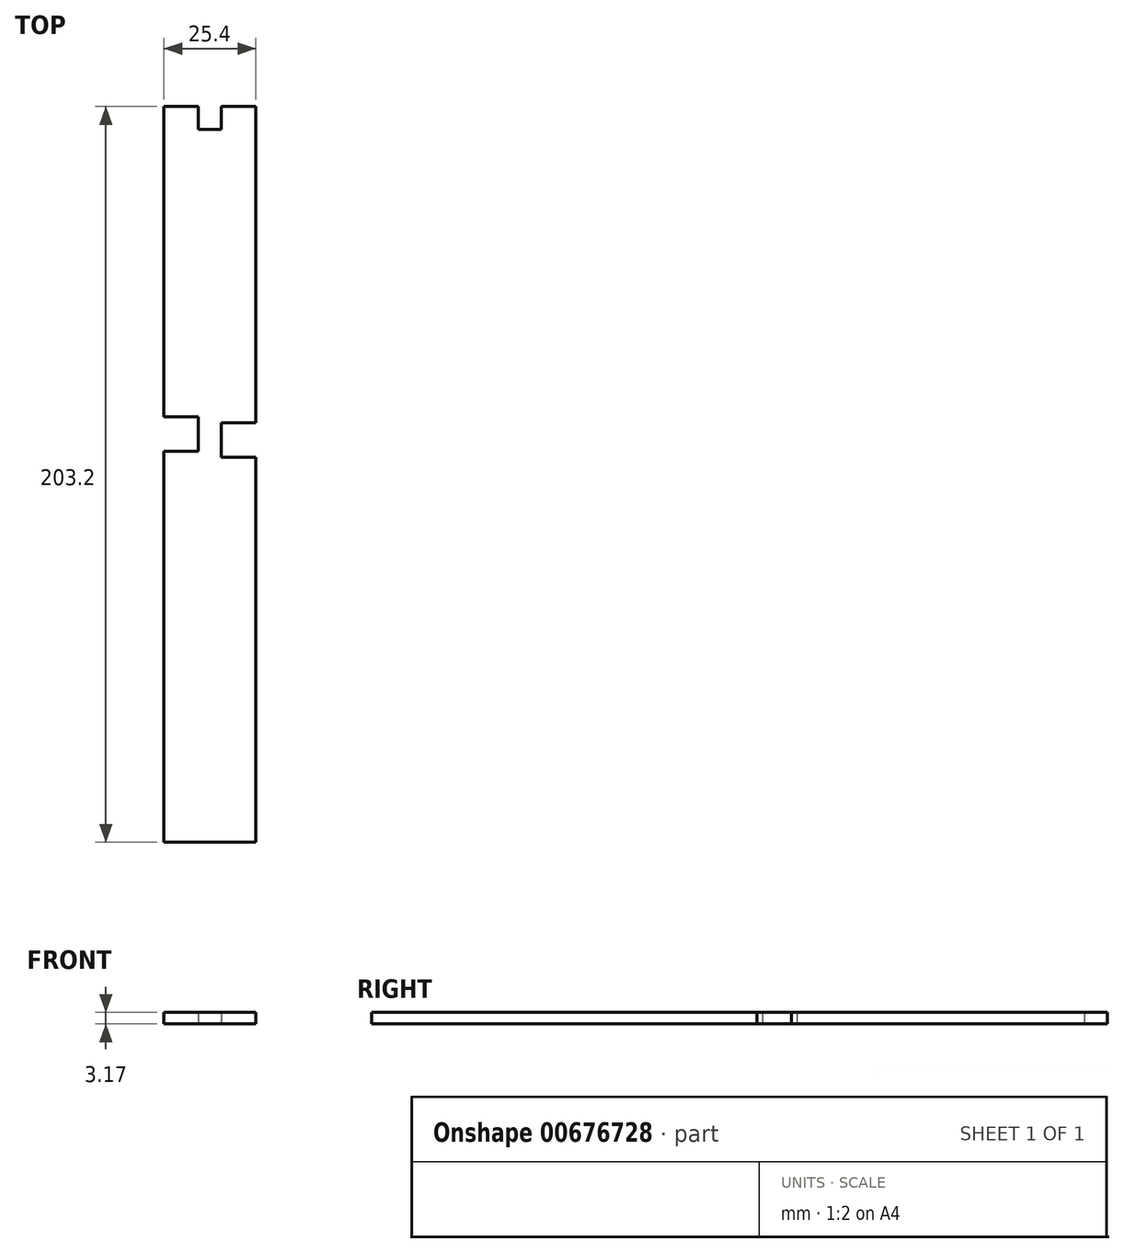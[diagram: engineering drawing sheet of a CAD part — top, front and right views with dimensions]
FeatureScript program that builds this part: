
annotation { "Feature Type Name" : "Feature", "Feature Type Description" : "" }
export const myFeature = defineFeature(function(context is Context, id is Id, definition is map)
    precondition{}
    {
        {
            var Q0;
            Q0=qCreatedBy(makeId("Top.planeOp"),FACE);
            var sketch = newSketch(context, id + "F0", { "sketchPlane" : qUnion([Q0])});
            skLineSegment(sketch, "E0.bottom", {"start": v(-12.7, -101.6) * mm, "end": v(12.7, -101.6) * mm});
            skLineSegment(sketch, "E0.top", {"start": v(-12.7, 101.6) * mm, "end": v(12.7, 101.6) * mm});
            skLineSegment(sketch, "E0.left", {"start": v(-12.7, -101.6) * mm, "end": v(-12.7, 101.6) * mm});
            skLineSegment(sketch, "E0.right", {"start": v(12.7, -101.6) * mm, "end": v(12.7, 101.6) * mm});
            skPoint(sketch, "E0.middle", {"position": v(0, 0) * mm});
            skLineSegment(sketch, "E1.bottom", {"start": v(-3.17, 101.6) * mm, "end": v(3.18, 101.6) * mm});
            skLineSegment(sketch, "E1.top", {"start": v(-3.17, 95.25) * mm, "end": v(3.18, 95.25) * mm});
            skLineSegment(sketch, "E1.left", {"start": v(-3.18, 101.6) * mm, "end": v(-3.18, 95.25) * mm});
            skLineSegment(sketch, "E1.right", {"start": v(3.18, 101.6) * mm, "end": v(3.18, 95.25) * mm});
            skLineSegment(sketch, "E2.bottom", {"start": v(12.7, 14.29) * mm, "end": v(3.18, 14.29) * mm});
            skLineSegment(sketch, "E2.top", {"start": v(12.7, 4.76) * mm, "end": v(3.18, 4.76) * mm});
            skLineSegment(sketch, "E2.left", {"start": v(12.7, 14.29) * mm, "end": v(12.7, 4.76) * mm});
            skLineSegment(sketch, "E2.right", {"start": v(3.18, 14.29) * mm, "end": v(3.18, 4.76) * mm});
            skLineSegment(sketch, "E3.bottom", {"start": v(-12.7, 15.87) * mm, "end": v(-3.17, 15.87) * mm});
            skLineSegment(sketch, "E3.top", {"start": v(-12.7, 6.35) * mm, "end": v(-3.17, 6.35) * mm});
            skLineSegment(sketch, "E3.left", {"start": v(-12.7, 15.87) * mm, "end": v(-12.7, 6.35) * mm});
            skLineSegment(sketch, "E3.right", {"start": v(-3.17, 15.87) * mm, "end": v(-3.17, 6.35) * mm});
            skSolve(sketch);
        }
        {
            var Q0;
            {var subQ7=sQuery(id+"F0.wireOp",EDGE,"E0.bottom");Q0=makeQuery(id+"F0.imprint","IMPRINT",FACE,{"disambiguationData":[TD([[makeQuery(id+"F0.imprint","IMPRINT",EDGE,{"derivedFrom":subQ7}),1.0]])]});}
            extrude(context, id + "F1", {"entities" : qUnion([Q0]), "depth" : 3.17 * mm, "offsetDistance" : 25.4 * mm});
        }
    });
